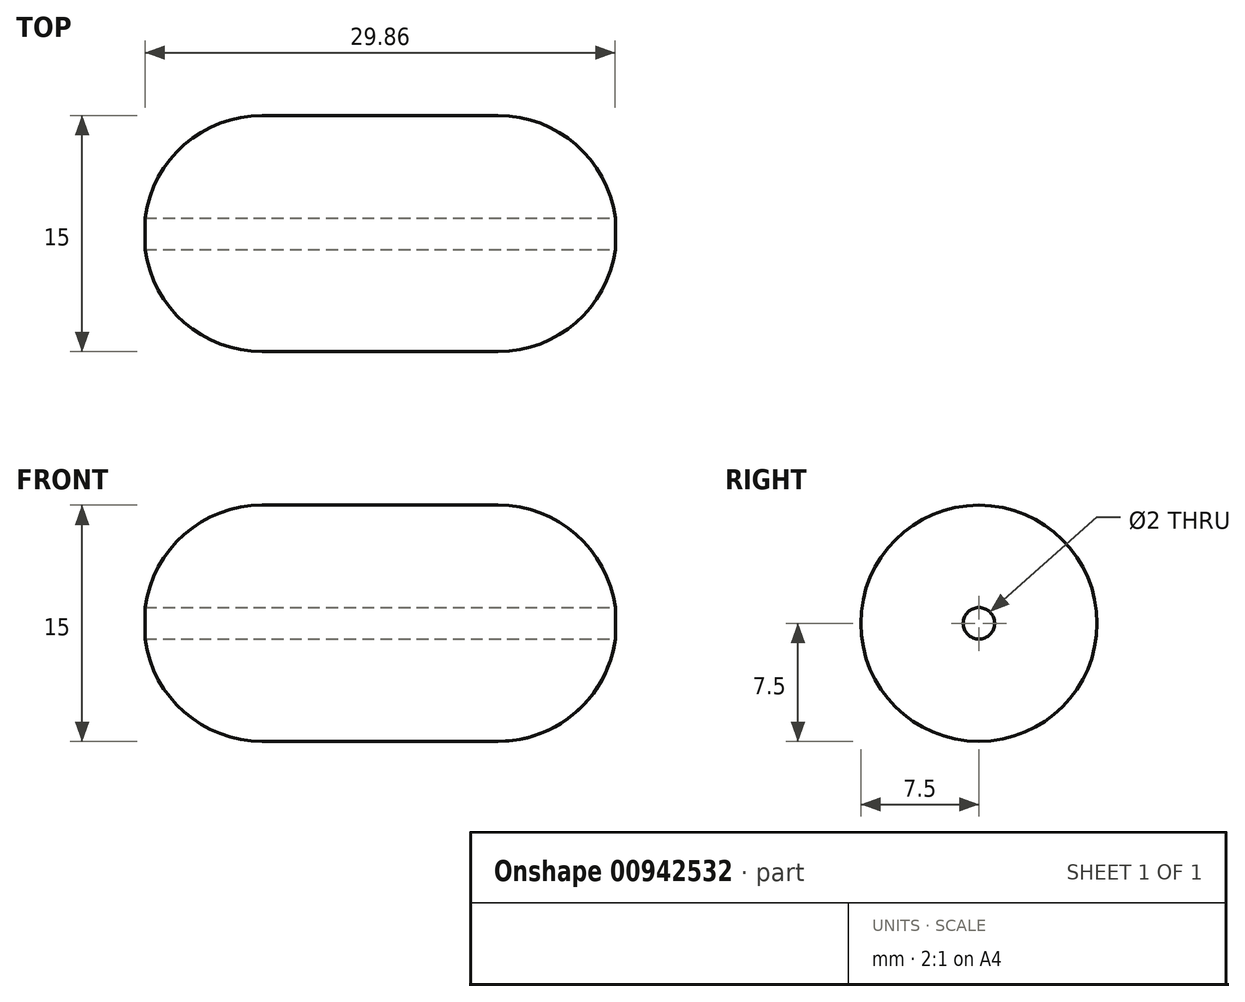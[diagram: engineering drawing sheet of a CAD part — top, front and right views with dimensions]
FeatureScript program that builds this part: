
annotation { "Feature Type Name" : "Feature", "Feature Type Description" : "" }
export const myFeature = defineFeature(function(context is Context, id is Id, definition is map)
    precondition{}
    {
        {
            var Q0;
            Q0=qCreatedBy(makeId("Front.planeOp"),FACE);
            var sketch = newSketch(context, id + "F0", { "sketchPlane" : qUnion([Q0])});
            skLineSegment(sketch, "E0.bottom", {"start": v(15, -7.5) * mm, "end": v(-15, -7.5) * mm});
            skLineSegment(sketch, "E0.top", {"start": v(15, 7.5) * mm, "end": v(-15, 7.5) * mm});
            skLineSegment(sketch, "E0.left", {"start": v(15, -7.5) * mm, "end": v(15, 7.5) * mm});
            skLineSegment(sketch, "E0.right", {"start": v(-15, -7.5) * mm, "end": v(-15, 7.5) * mm});
            skPoint(sketch, "E0.middle", {"position": v(0, 0) * mm});
            skSolve(sketch);
        }
        {
            var Q0;
            Q0=makeQuery(id+"F0.imprint","IMPRINT",FACE,{"disambiguationData":[TD([[makeQuery(id+"F0.imprint","IMPRINT",EDGE,{"derivedFrom":sQuery(id+"F0.wireOp",EDGE,"E0.bottom")}),-1.0]])]});
            extrude(context, id + "F1", {"entities" : qUnion([Q0]), "depth" : 7.5 * mm, "offsetDistance" : 25 * mm, "hasSecondDirection" : true, "secondDirectionOppositeDirection" : true, "secondDirectionDepth" : 7.5 * mm});
        }
        {
            var Q0;
            Q0=makeQuery(id+"F1.opExtrude","CAP_EDGE",EDGE,{"disambiguationData":[OSD([sQuery(id+"F0.wireOp",EDGE,"E0.top")])],"isStart":false});
            var Q1;
            Q1=makeQuery(id+"F1.opExtrude","CAP_EDGE",EDGE,{"disambiguationData":[OSD([sQuery(id+"F0.wireOp",EDGE,"E0.top")])],"isStart":true});
            var Q2;
            Q2=makeQuery(id+"F1.opExtrude","CAP_EDGE",EDGE,{"disambiguationData":[OSD([sQuery(id+"F0.wireOp",EDGE,"E0.bottom")])],"isStart":true});
            var Q3;
            Q3=makeQuery(id+"F1.opExtrude","SWEPT_EDGE",EDGE,{"disambiguationData":[OSD([sQuery(id+"F0.wireOp",EDGE,"E0.top"),sQuery(id+"F0.wireOp",EDGE,"E0.right")])]});
            var Q4;
            Q4=makeQuery(id+"F1.opExtrude","CAP_EDGE",EDGE,{"disambiguationData":[OSD([sQuery(id+"F0.wireOp",EDGE,"E0.right")])],"isStart":true});
            var Q5;
            Q5=makeQuery(id+"F1.opExtrude","CAP_EDGE",EDGE,{"disambiguationData":[OSD([sQuery(id+"F0.wireOp",EDGE,"E0.right")])],"isStart":false});
            var Q6;
            Q6=makeQuery(id+"F1.opExtrude","CAP_EDGE",EDGE,{"disambiguationData":[OSD([sQuery(id+"F0.wireOp",EDGE,"E0.left")])],"isStart":false});
            var Q7;
            Q7=makeQuery(id+"F1.opExtrude","SWEPT_EDGE",EDGE,{"disambiguationData":[OSD([sQuery(id+"F0.wireOp",EDGE,"E0.top"),sQuery(id+"F0.wireOp",EDGE,"E0.left")])]});
            var Q8;
            Q8=makeQuery(id+"F1.opExtrude","CAP_EDGE",EDGE,{"disambiguationData":[OSD([sQuery(id+"F0.wireOp",EDGE,"E0.left")])],"isStart":true});
            var Q9;
            Q9=makeQuery(id+"F1.opExtrude","CAP_EDGE",EDGE,{"disambiguationData":[OSD([sQuery(id+"F0.wireOp",EDGE,"E0.bottom")])],"isStart":false});
            var Q10;
            Q10=makeQuery(id+"F1.opExtrude","SWEPT_EDGE",EDGE,{"disambiguationData":[OSD([sQuery(id+"F0.wireOp",EDGE,"E0.bottom"),sQuery(id+"F0.wireOp",EDGE,"E0.left")])]});
            var Q11;
            Q11=makeQuery(id+"F1.opExtrude","SWEPT_EDGE",EDGE,{"disambiguationData":[OSD([sQuery(id+"F0.wireOp",EDGE,"E0.bottom"),sQuery(id+"F0.wireOp",EDGE,"E0.right")])]});
            fillet(context, id + "F2", {"entities" : qUnion([Q0, Q1, Q2, Q3, Q4, Q5, Q6, Q7, Q8, Q9, Q10, Q11]), "tangentPropagation" : true, "radius" : 7.5 * mm, "defaultsChanged" : false, "vertexSettings" : [], "allowEdgeOverflow" : false});
        }
        {
            var Q0;
            Q0=qCreatedBy(makeId("Right.planeOp"),FACE);
            var sketch = newSketch(context, id + "F3", { "sketchPlane" : qUnion([Q0])});
            skCircle(sketch, "E1", {"center": v(0, 0) * mm, "radius": 1 * mm});
            skSolve(sketch);
        }
        {
            var Q0;
            Q0=makeQuery(id+"F3.imprint","IMPRINT",FACE,{"disambiguationData":[TD([[makeQuery(id+"F3.imprint","IMPRINT",EDGE,{"derivedFrom":sQuery(id+"F3.wireOp",EDGE,"E1")}),1.0]])]});
            extrude(context, id + "F4", {"entities" : qUnion([Q0]), "operationType" : NewBodyOperationType.REMOVE, "oppositeDirection" : true, "depth" : 50 * mm, "offsetDistance" : 25 * mm, "hasSecondDirection" : true, "secondDirectionOppositeDirection" : false, "secondDirectionDepth" : 50 * mm});
        }
    });
